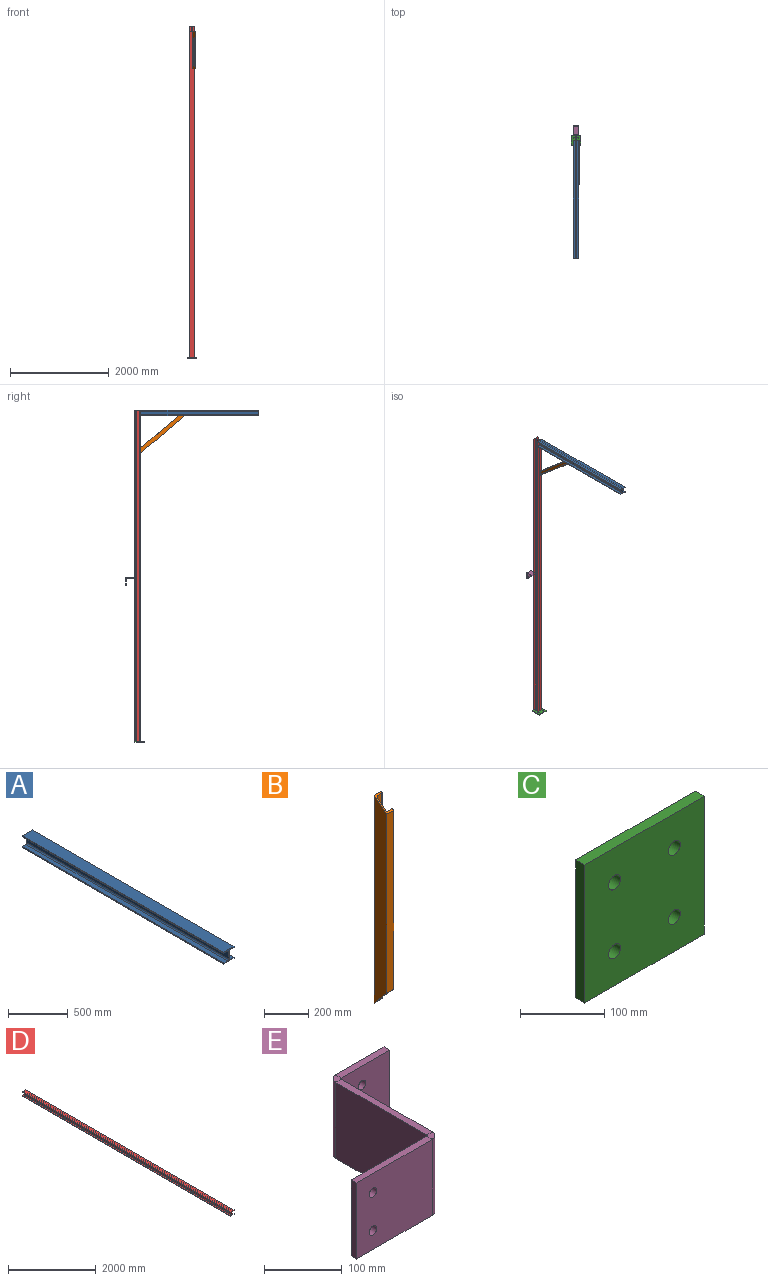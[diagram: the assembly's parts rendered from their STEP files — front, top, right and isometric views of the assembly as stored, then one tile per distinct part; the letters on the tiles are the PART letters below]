
ASSEMBLY  parts=5 mates=4
PART A: 18 faces, bbox 120x2380x120 mm
  f0: cylinder r=12mm len=2380mm, axis (0,-1,0), area 44861.9mm2, adj f7,f8,f16,f17
  f1: cylinder r=12mm len=2380mm, axis (0,-1,0), area 44861.9mm2, adj f8,f9,f16,f17
  f2: cylinder r=12mm len=2380mm, axis (0,-1,0), area 44861.9mm2, adj f13,f14,f16,f17
  f3: cylinder r=12mm len=2380mm, axis (0,-1,0), area 44861.9mm2, adj f14,f15,f16,f17
  f4: plane 2380x11mm, normal (-1,0,0), area 26180mm2, adj f5,f15,f16,f17
  f5: plane 2380x120mm, normal (0,0,-1), area 285600mm2, adj f4,f6,f16,f17
  f6: plane 2380x11mm, normal (1,0,0), area 26180mm2, adj f5,f7,f16,f17
  f7: plane 2380x44.75mm, normal (0,0,1), area 106505mm2, adj f0,f6,f16,f17
  f8: plane 2380x74mm, normal (1,0,0), area 176120mm2, adj f0,f1,f16,f17
  f9: plane 2380x44.75mm, normal (0,0,-1), area 106505mm2, adj f1,f10,f16,f17
  f10: plane 2380x11mm, normal (1,0,0), area 26180mm2, adj f9,f11,f16,f17
  f11: plane 2380x120mm, normal (0,0,1), area 285600mm2, adj f10,f12,f16,f17
  f12: plane 2380x11mm, normal (-1,0,0), area 26180mm2, adj f11,f13,f16,f17
  f13: plane 2380x44.75mm, normal (0,0,-1), area 106505mm2, adj f2,f12,f16,f17
  f14: plane 2380x74mm, normal (-1,0,0), area 176120mm2, adj f2,f3,f16,f17
  f15: plane 2380x44.75mm, normal (0,0,1), area 106505mm2, adj f3,f4,f16,f17
  f16: plane 120x120mm, normal (0,1,0), area 3400.6mm2, adj f0,f1,f2,f3,f4,f5,f6,f7
  f17: plane 120x120mm, normal (0,-1,0), area 3400.6mm2, adj f0,f1,f2,f3,f4,f5,f6,f7
PART B: 14 faces, bbox 47.4x82.4x1158.6 mm
  f0: plane 96.23x82.36mm, normal (0,-0.76,-0.65), area 1740mm2, adj f1,f2,f3,f4,f5,f6,f7,f8
  f1: cylinder r=4mm len=1149.15mm, axis (0,0,1), area 7194.9mm2, adj f0,f2,f12,f13
  f2: plane 1141.05x27mm, normal (0.04,-1,0), area 30802.1mm2, adj f0,f1,f3,f13
  f3: cylinder r=8mm len=1139.02mm, axis (0,0,1), area 14239.5mm2, adj f0,f2,f4,f13
  f4: plane 1122.82x47mm, normal (1,0,0), area 50535.1mm2, adj f0,f3,f5,f13
  f5: cylinder r=8mm len=1027.61mm, axis (0,0,1), area 12783.7mm2, adj f0,f4,f6,f13
  f6: plane 1011.41x27mm, normal (0.04,1,0), area 27299.4mm2, adj f0,f5,f7,f13
  f7: cylinder r=4mm len=1009.38mm, axis (0,0,1), area 6316.7mm2, adj f0,f6,f8,f13
  f8: plane 1001.28x3.5mm, normal (1,0,0), area 3492.1mm2, adj f0,f7,f9,f13
  f9: plane 994.19x45mm, normal (0,-1,0), area 44738.6mm2, adj f0,f8,f10,f13
  f10: plane 1156.24x80mm, normal (-1,0,0), area 86017.3mm2, adj f0,f9,f11,f13
  f11: plane 1156.24x45mm, normal (0,1,0), area 52030.8mm2, adj f0,f10,f12,f13
  f12: plane 1156.24x3.5mm, normal (1,0,0), area 4034.4mm2, adj f0,f1,f11,f13
  f13: plane 81.52x69.7mm, normal (0,-0.65,0.76), area 1484.3mm2, adj f1,f2,f3,f4,f5,f6,f7,f8
PART C: 10 faces, bbox 200x15x200 mm
  f0: plane 200x15mm, normal (0,0,-1), area 3000mm2, adj f1,f7,f8,f9
  f1: plane 200x15mm, normal (1,0,0), area 3000mm2, adj f0,f2,f8,f9
  f2: plane 200x15mm, normal (0,0,1), area 3000mm2, adj f1,f7,f8,f9
  f3: cylinder r=10mm len=20mm, axis (0,1,0), area 942.5mm2, adj f8,f9
  f4: cylinder r=10mm len=20mm, axis (0,1,0), area 942.5mm2, adj f8,f9
  f5: cylinder r=10mm len=20mm, axis (0,1,0), area 942.5mm2, adj f8,f9
  f6: cylinder r=10mm len=20mm, axis (0,1,0), area 942.5mm2, adj f8,f9
  f7: plane 200x15mm, normal (-1,0,0), area 3000mm2, adj f0,f2,f8,f9
  f8: plane 200x200mm, normal (0,-1,0), area 38743.4mm2, adj f0,f1,f2,f3,f4,f5,f6,f7
  f9: plane 200x200mm, normal (0,1,0), area 38743.4mm2, adj f0,f1,f2,f3,f4,f5,f6,f7
PART D: 18 faces, bbox 120x6705x120 mm
  f0: plane 6705x11mm, normal (-1,0,0), area 73755mm2, adj f1,f14,f15,f16
  f1: plane 6705x120mm, normal (0,0,-1), area 804600mm2, adj f0,f2,f14,f16
  f2: plane 6705x11mm, normal (1,0,0), area 73755mm2, adj f1,f3,f14,f16
  f3: plane 6705x44.75mm, normal (0,0,1), area 300048.8mm2, adj f2,f4,f14,f16
  f4: cylinder r=12mm len=6705mm, axis (0,-1,0), area 126386.3mm2, adj f3,f5,f14,f16
  f5: plane 6705x74mm, normal (1,0,0), area 496170mm2, adj f4,f6,f14,f16
  f6: cylinder r=12mm len=6705mm, axis (0,-1,0), area 126386.3mm2, adj f5,f7,f14,f16
  f7: plane 6705x44.75mm, normal (0,0,-1), area 300048.8mm2, adj f6,f8,f14,f16
  f8: plane 6705x11mm, normal (1,0,0), area 73755mm2, adj f7,f9,f14,f16
  f9: plane 6705x120mm, normal (0,0,1), area 804600mm2, adj f8,f10,f14,f16
  f10: plane 6705x11mm, normal (-1,0,0), area 73755mm2, adj f9,f11,f14,f16
  f11: plane 6705x44.75mm, normal (0,0,-1), area 300048.8mm2, adj f10,f12,f14,f16
  f12: cylinder r=12mm len=6705mm, axis (0,-1,0), area 126386.3mm2, adj f11,f13,f14,f16
  f13: plane 6705x74mm, normal (-1,0,0), area 496170mm2, adj f12,f14,f16,f17
  f14: plane 120x120mm, normal (0,-1,0), area 3400.6mm2, adj f0,f1,f2,f3,f4,f5,f6,f7
  f15: plane 6705x44.75mm, normal (0,0,1), area 300048.8mm2, adj f0,f14,f16,f17
  f16: plane 120x120mm, normal (0,1,0), area 3400.6mm2, adj f0,f1,f2,f3,f4,f5,f6,f7
  f17: cylinder r=12mm len=6705mm, axis (0,-1,0), area 126386.3mm2, adj f13,f14,f15,f16
PART E: 26 faces, bbox 240x190x120 mm
  f0: plane 138x10mm, normal (0,0,-1), area 1380mm2, adj f1,f5,f6,f23
  f1: plane 120x10mm, normal (-1,0,0), area 1200mm2, adj f0,f2,f5,f6
  f2: plane 138x10mm, normal (0,0,1), area 1380mm2, adj f1,f5,f6,f22
  f3: cylinder r=7mm len=14mm, axis (0,-1,0), area 439.8mm2, adj f5,f6
  f4: cylinder r=7mm len=14mm, axis (0,-1,0), area 439.8mm2, adj f5,f6
  f5: plane 138x120mm, normal (0,1,0), area 16252.1mm2, adj f0,f1,f2,f3,f4,f25
  f6: plane 138x120mm, normal (0,-1,0), area 16252.1mm2, adj f0,f1,f2,f3,f4,f24
  f7: plane 166x10mm, normal (0,0,-1), area 1660mm2, adj f9,f10,f19,f23
  f8: plane 166x10mm, normal (0,0,1), area 1660mm2, adj f9,f10,f18,f22
  f9: plane 166x120mm, normal (-1,0,0), area 19920mm2, adj f7,f8,f20,f25
  f10: plane 166x120mm, normal (1,0,0), area 19920mm2, adj f7,f8,f21,f24
  f11: plane 88x10mm, normal (0,0,-1), area 880mm2, adj f15,f16,f17,f19
  f12: plane 88x10mm, normal (0,0,1), area 880mm2, adj f15,f16,f17,f18
  f13: cylinder r=7mm len=14mm, axis (0,1,0), area 439.8mm2, adj f16,f17
  f14: cylinder r=7mm len=14mm, axis (0,1,0), area 439.8mm2, adj f16,f17
  f15: plane 120x10mm, normal (1,0,0), area 1200mm2, adj f11,f12,f16,f17
  f16: plane 120x88mm, normal (0,1,0), area 10252.1mm2, adj f11,f12,f13,f14,f15,f20
  f17: plane 120x88mm, normal (0,-1,0), area 10252.1mm2, adj f11,f12,f13,f14,f15,f21
  f18: plane 12x12mm, normal (0,0,1), area 110mm2, adj f8,f12,f20,f21
  f19: plane 12x12mm, normal (0,0,-1), area 110mm2, adj f7,f11,f20,f21
  f20: cylinder r=12mm len=120mm, axis (0,0,1), area 2261.9mm2, adj f9,f16,f18,f19
  f21: cylinder r=2mm len=120mm, axis (0,0,1), area 377mm2, adj f10,f17,f18,f19
  f22: plane 12x12mm, normal (0,0,1), area 110mm2, adj f2,f8,f24,f25
  f23: plane 12x12mm, normal (0,0,-1), area 110mm2, adj f0,f7,f24,f25
  f24: cylinder r=12mm len=120mm, axis (0,0,1), area 2261.9mm2, adj f6,f10,f22,f23
  f25: cylinder r=2mm len=120mm, axis (0,0,1), area 377mm2, adj f5,f9,f22,f23
PLACE A t=(817.22,-1359.69,5999.77)mm
PLACE B rot(axis=(-1,0,0),130.4deg) t=(894.9,-2187.63,6061)mm
PLACE C rot(axis=(-1,0,0),90deg) t=(877.52,-1339.69,-592.59)mm
PLACE D rot(axis=(1,0,0),90deg) t=(817.22,-1239.54,6119.91)mm
PLACE E rot(axis=(-0.71,0,-0.71),180deg) t=(817.52,-1059.69,2571.23)mm
MATE fastened D.f14 <-> C.f8  axis (0,0,-1) through (877.52,-1239.69,-585.09)mm
MATE fastened A.f16 <-> D.f9  axis (0,1,0) through (877.52,-1359.69,6119.91)mm
MATE planar B.f0 <-> A.f5  axis (0,0,1) through (918.46,-2239.69,5999.91)mm
MATE fastened E.f16 <-> D.f1  axis (0,-1,0) through (877.52,-1239.69,2767.41)mm
